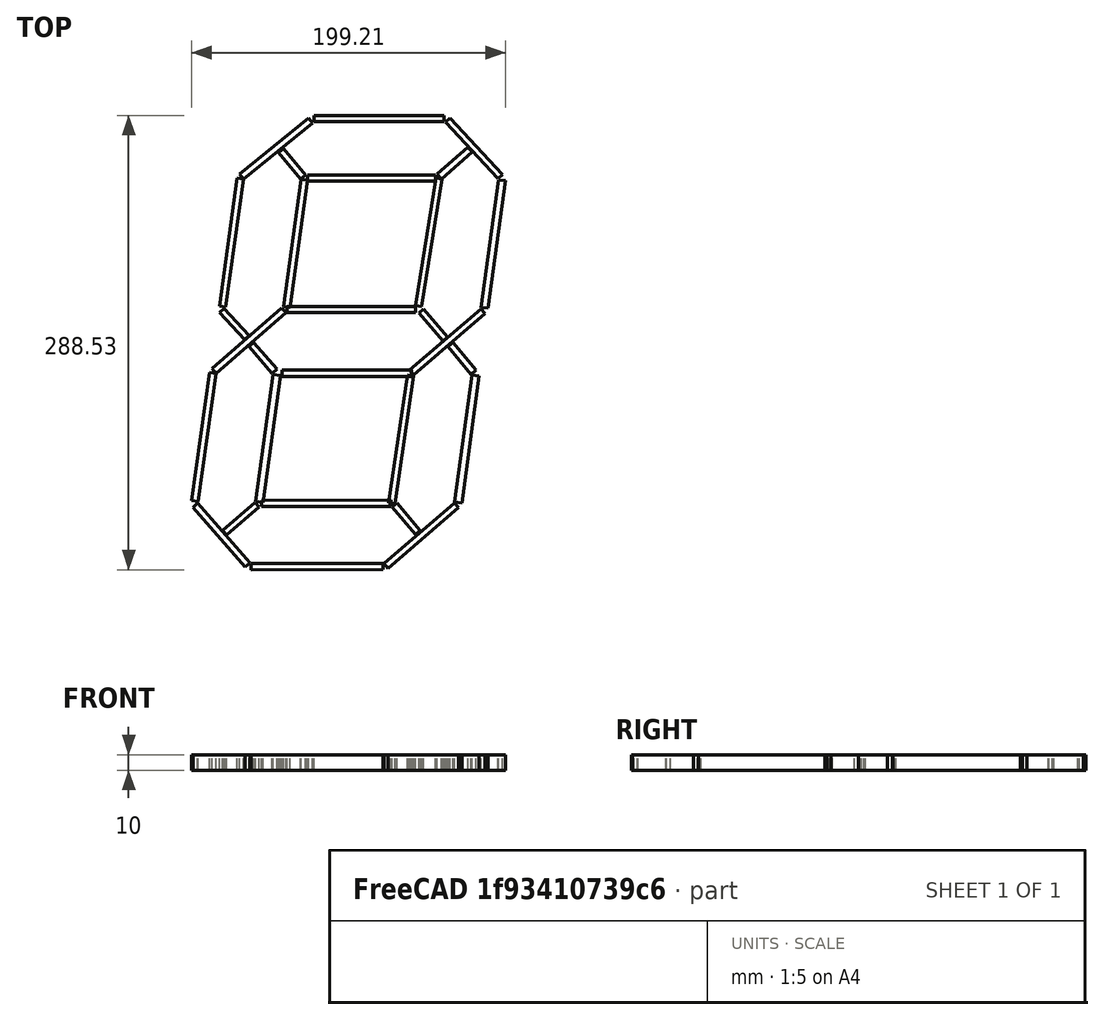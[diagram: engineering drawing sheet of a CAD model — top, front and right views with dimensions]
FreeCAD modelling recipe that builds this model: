
FCSTD DOCUMENT  (FreeCAD 0.18R16131 (Git))
Label: afficheur
License: All rights reserved
LicenseURL: http://en.wikipedia.org/wiki/All_rights_reserved
objects: Image::ImagePlane×1, Sketcher::SketchObject×1, PartDesign::Body×1, Part::Extrusion×1
note: 3 computed .brp shape members not serialized (recipe doc carries the construction recipe); baked Part::Feature solids carry a one-line shape summary decoded from their .brp

FEATURE [Image::ImagePlane] ImagePlane
  XSize = 210
  YSize = 297
FEATURE [Sketcher::SketchObject] Sketch
  MapMode = 5
  Support = -> [XY_Plane]
  sketch-geometry (112):
    g0: LineSegment StartX=-80.0528 StartY=21.6446 StartZ=0 EndX=-68.7891 EndY=102.867 EndZ=0
    g1: LineSegment StartX=-68.7891 StartY=102.867 StartZ=0 EndX=-72.7512 EndY=103.417 EndZ=0
    g2: LineSegment StartX=-72.7512 StartY=103.417 StartZ=0 EndX=-84.0149 EndY=22.1941 EndZ=0
    g3: LineSegment StartX=-84.0149 StartY=22.1941 StartZ=0 EndX=-80.0528 EndY=21.6446 EndZ=0
    g4: LineSegment StartX=-68.7891 StartY=102.867 StartZ=0 EndX=-24.7803 EndY=138.396 EndZ=0
    g5: LineSegment StartX=-24.7803 StartY=138.396 StartZ=0 EndX=-27.2929 EndY=141.508 EndZ=0
    g6: LineSegment StartX=-27.2929 StartY=141.508 StartZ=0 EndX=-71.3017 EndY=105.98 EndZ=0
    g7: LineSegment StartX=-71.3017 StartY=105.98 StartZ=0 EndX=-68.7891 EndY=102.867 EndZ=0
    g8: LineSegment StartX=-97.5888 StartY=-101.804 StartZ=0 EndX=-86.1106 EndY=-20.6108 EndZ=0
    g9: LineSegment StartX=-86.1106 StartY=-20.6108 StartZ=0 EndX=-90.0712 EndY=-20.0509 EndZ=0
    g10: LineSegment StartX=-90.0712 StartY=-20.0509 StartZ=0 EndX=-101.549 EndY=-101.244 EndZ=0
    g11: LineSegment StartX=-101.549 StartY=-101.244 StartZ=0 EndX=-97.5888 EndY=-101.804 EndZ=0
    g12: LineSegment StartX=-86.1106 StartY=-20.6108 StartZ=0 EndX=-41.7841 EndY=18.0739 EndZ=0
    g13: LineSegment StartX=-41.7841 StartY=18.0739 StartZ=0 EndX=-44.4143 EndY=21.0876 EndZ=0
    g14: LineSegment StartX=-44.4143 StartY=21.0876 StartZ=0 EndX=-88.7407 EndY=-17.5971 EndZ=0
    g15: LineSegment StartX=-88.7407 StartY=-17.5971 StartZ=0 EndX=-86.1106 EndY=-20.6108 EndZ=0
    g16: LineSegment StartX=44.4454 StartY=22.0114 StartZ=0 EndX=57.4126 EndY=102.98 EndZ=0
    g17: LineSegment StartX=57.4126 StartY=102.98 StartZ=0 EndX=53.4629 EndY=103.612 EndZ=0
    g18: LineSegment StartX=53.4629 StartY=103.612 StartZ=0 EndX=40.4957 EndY=22.6439 EndZ=0
    g19: LineSegment StartX=40.4957 StartY=22.6439 StartZ=0 EndX=44.4454 EndY=22.0114 EndZ=0
    g20: LineSegment StartX=27.5517 StartY=-103.318 StartZ=0 EndX=39.3566 EndY=-22.1724 EndZ=0
    g21: LineSegment StartX=39.3566 StartY=-22.1724 StartZ=0 EndX=35.3983 EndY=-21.5965 EndZ=0
    g22: LineSegment StartX=35.3983 StartY=-21.5965 StartZ=0 EndX=23.5934 EndY=-102.742 EndZ=0
    g23: LineSegment StartX=23.5934 StartY=-102.742 StartZ=0 EndX=27.5517 EndY=-103.318 EndZ=0
    g24: LineSegment StartX=39.4539 StartY=-21.4329 StartZ=0 EndX=84.758 EndY=17.4459 EndZ=0
    g25: LineSegment StartX=84.758 StartY=17.4459 StartZ=0 EndX=82.153 EndY=20.4814 EndZ=0
    g26: LineSegment StartX=82.153 StartY=20.4814 StartZ=0 EndX=36.8489 EndY=-18.3974 EndZ=0
    g27: LineSegment StartX=36.8489 StartY=-18.3974 StartZ=0 EndX=39.4539 EndY=-21.4329 EndZ=0
    g28: LineSegment StartX=-46.4 StartY=119.697 StartZ=0 EndX=-43.3361 EndY=122.268 EndZ=0
    g29: LineSegment StartX=-43.3361 StartY=122.268 StartZ=0 EndX=-29.2643 EndY=105.501 EndZ=0
    g30: LineSegment StartX=-29.2643 StartY=105.501 StartZ=0 EndX=-32.3282 EndY=102.93 EndZ=0
    g31: LineSegment StartX=-32.3282 StartY=102.93 StartZ=0 EndX=-46.4 EndY=119.697 EndZ=0
    g32: LineSegment StartX=42.7184 StartY=17.7806 StartZ=0 EndX=45.757 EndY=20.382 EndZ=0
    g33: LineSegment StartX=45.757 StartY=20.382 StartZ=0 EndX=60.9792 EndY=2.60137 EndZ=0
    g34: LineSegment StartX=60.9792 StartY=2.60137 StartZ=0 EndX=57.9407 EndY=0 EndZ=0
    g35: LineSegment StartX=57.9407 StartY=0 StartZ=0 EndX=42.7184 EndY=17.7806 EndZ=0
    g36: LineSegment StartX=-65.1983 StartY=-3.41341 StartZ=0 EndX=-62.1657 EndY=-0.805122 EndZ=0
    g37: LineSegment StartX=-62.1657 StartY=-0.805122 StartZ=0 EndX=-47.4642 EndY=-17.8984 EndZ=0
    g38: LineSegment StartX=-47.4642 StartY=-17.8984 StartZ=0 EndX=-50.4969 EndY=-20.5067 EndZ=0
    g39: LineSegment StartX=-50.4969 StartY=-20.5067 StartZ=0 EndX=-65.1983 EndY=-3.41341 EndZ=0
    g40: LineSegment StartX=61.1912 StartY=-3.50708 StartZ=0 EndX=64.2552 EndY=-0.935642 EndZ=0
    g41: LineSegment StartX=64.2552 StartY=-0.935642 StartZ=0 EndX=79.019 EndY=-18.5271 EndZ=0
    g42: LineSegment StartX=79.019 StartY=-18.5271 StartZ=0 EndX=75.955 EndY=-21.0985 EndZ=0
    g43: LineSegment StartX=75.955 StartY=-21.0985 StartZ=0 EndX=61.1912 EndY=-3.50708 EndZ=0
    g44: LineSegment StartX=25.7044 StartY=-105.315 StartZ=0 EndX=28.7683 EndY=-102.743 EndZ=0
    g45: LineSegment StartX=28.7683 StartY=-102.743 StartZ=0 EndX=43.5321 EndY=-120.335 EndZ=0
    g46: LineSegment StartX=43.5321 StartY=-120.335 StartZ=0 EndX=40.4682 EndY=-122.906 EndZ=0
    g47: LineSegment StartX=40.4682 StartY=-122.906 StartZ=0 EndX=25.7044 EndY=-105.315 EndZ=0
    g48: LineSegment StartX=-83.8754 StartY=17.9786 StartZ=0 EndX=-80.9281 EndY=20.683 EndZ=0
    g49: LineSegment StartX=-80.9281 StartY=20.683 StartZ=0 EndX=-65.206 EndY=3.54857 EndZ=0
    g50: LineSegment StartX=-65.206 StartY=3.54857 StartZ=0 EndX=-68.1533 EndY=0.844226 EndZ=0
    g51: LineSegment StartX=-68.1533 StartY=0.844226 StartZ=0 EndX=-83.8754 EndY=17.9786 EndZ=0
    g52: LineSegment StartX=-56.3952 StartY=-102.565 StartZ=0 EndX=-45.2429 EndY=-21.8493 EndZ=0
    g53: LineSegment StartX=-45.2429 StartY=-21.8493 StartZ=0 EndX=-49.8266 EndY=-21.216 EndZ=0
    g54: LineSegment StartX=-49.8266 StartY=-21.216 StartZ=0 EndX=-60.9789 EndY=-101.932 EndZ=0
    g55: LineSegment StartX=-60.9789 StartY=-101.932 StartZ=0 EndX=-56.3952 EndY=-102.565 EndZ=0
    g56: LineSegment StartX=69.9748 StartY=-102.706 StartZ=0 EndX=80.8261 EndY=-22.2952 EndZ=0
    g57: LineSegment StartX=80.8261 StartY=-22.2952 StartZ=0 EndX=76.3147 EndY=-21.6864 EndZ=0
    g58: LineSegment StartX=76.3147 StartY=-21.6864 StartZ=0 EndX=65.4635 EndY=-102.097 EndZ=0
    g59: LineSegment StartX=65.4635 StartY=-102.097 StartZ=0 EndX=69.9748 EndY=-102.706 EndZ=0
    g60: LineSegment StartX=-39.2627 StartY=21.4194 StartZ=0 EndX=-28.1746 EndY=102.11 EndZ=0
    g61: LineSegment StartX=-28.1746 StartY=102.11 StartZ=0 EndX=-32.1374 EndY=102.655 EndZ=0
    g62: LineSegment StartX=-32.1374 StartY=102.655 StartZ=0 EndX=-43.2254 EndY=21.964 EndZ=0
    g63: LineSegment StartX=-43.2254 StartY=21.964 StartZ=0 EndX=-39.2627 EndY=21.4194 EndZ=0
    g64: LineSegment StartX=86.4927 StartY=20.8333 StartZ=0 EndX=97.66 EndY=101.812 EndZ=0
    g65: LineSegment StartX=97.66 StartY=101.812 StartZ=0 EndX=93.3498 EndY=102.406 EndZ=0
    g66: LineSegment StartX=93.3498 StartY=102.406 StartZ=0 EndX=82.1825 EndY=21.4277 EndZ=0
    g67: LineSegment StartX=82.1825 StartY=21.4277 StartZ=0 EndX=86.4927 EndY=20.8333 EndZ=0
    g68: LineSegment StartX=23.1509 StartY=-144.428 StartZ=0 EndX=67.908 EndY=-105.772 EndZ=0
    g69: LineSegment StartX=65.2934 StartY=-102.744 StartZ=0 EndX=20.5363 EndY=-141.401 EndZ=0
    g70: LineSegment StartX=20.5363 StartY=-141.401 StartZ=0 EndX=23.1509 EndY=-144.428 EndZ=0
    g71: LineSegment StartX=67.908 StartY=-105.772 StartZ=0 EndX=65.2934 EndY=-102.744 EndZ=0
    g72: LineSegment StartX=-97.7878 StartY=-102.928 StartZ=0 EndX=-100.805 EndY=-105.554 EndZ=0
    g73: LineSegment StartX=-64.6334 StartY=-141.017 StartZ=0 EndX=-97.7878 EndY=-102.928 EndZ=0
    g74: LineSegment StartX=-100.805 StartY=-105.554 StartZ=0 EndX=-67.6505 EndY=-143.643 EndZ=0
    g75: LineSegment StartX=-67.6505 StartY=-143.643 StartZ=0 EndX=-64.6334 EndY=-141.017 EndZ=0
    g76: LineSegment StartX=-81.926 StartY=-120.298 StartZ=0 EndX=-61.4802 EndY=-102.465 EndZ=0
    g77: LineSegment StartX=-61.4802 StartY=-102.465 StartZ=0 EndX=-58.851 EndY=-105.479 EndZ=0
    g78: LineSegment StartX=-79.2967 StartY=-123.312 StartZ=0 EndX=-81.926 EndY=-120.298 EndZ=0
    g79: LineSegment StartX=-58.851 StartY=-105.479 StartZ=0 EndX=-79.2967 EndY=-123.312 EndZ=0
    g80: LineSegment StartX=59.6818 StartY=138.989 StartZ=0 EndX=92.8609 EndY=103.131 EndZ=0
    g81: LineSegment StartX=95.7969 StartY=105.848 StartZ=0 EndX=62.6177 EndY=141.706 EndZ=0
    g82: LineSegment StartX=62.6177 StartY=141.706 StartZ=0 EndX=59.6818 EndY=138.989 EndZ=0
    g83: LineSegment StartX=92.8609 StartY=103.131 StartZ=0 EndX=95.7969 EndY=105.848 EndZ=0
    g84: LineSegment StartX=-23.9018 StartY=139.268 StartZ=0 EndX=58.5026 EndY=139.294 EndZ=0
    g85: LineSegment StartX=58.5013 StartY=143.294 StartZ=0 EndX=-23.9031 EndY=143.268 EndZ=0
    g86: LineSegment StartX=-23.9031 StartY=143.268 StartZ=0 EndX=-23.9018 EndY=139.268 EndZ=0
    g87: LineSegment StartX=58.5026 StartY=139.294 StartZ=0 EndX=58.5013 EndY=143.294 EndZ=0
    g88: LineSegment StartX=-28.0827 StartY=101.499 StartZ=0 EndX=53.3052 EndY=101.525 EndZ=0
    g89: LineSegment StartX=53.3039 StartY=105.525 StartZ=0 EndX=-28.084 EndY=105.499 EndZ=0
    g90: LineSegment StartX=-28.084 StartY=105.499 StartZ=0 EndX=-28.0827 EndY=101.499 EndZ=0
    g91: LineSegment StartX=53.3052 StartY=101.525 StartZ=0 EndX=53.3039 EndY=105.525 EndZ=0
    g92: LineSegment StartX=-41.057 StartY=18.0798 StartZ=0 EndX=40.6428 EndY=17.9939 EndZ=0
    g93: LineSegment StartX=40.6471 StartY=21.9939 StartZ=0 EndX=-41.0528 EndY=22.0798 EndZ=0
    g94: LineSegment StartX=-41.0528 StartY=22.0798 StartZ=0 EndX=-41.057 EndY=18.0798 EndZ=0
    g95: LineSegment StartX=40.6428 StartY=17.9939 StartZ=0 EndX=40.6471 EndY=21.9939 EndZ=0
    g96: LineSegment StartX=-44.345 StartY=-22.4905 StartZ=0 EndX=38.0594 EndY=-22.464 EndZ=0
    g97: LineSegment StartX=38.0581 StartY=-18.464 StartZ=0 EndX=-44.3463 EndY=-18.4905 EndZ=0
    g98: LineSegment StartX=-44.3463 StartY=-18.4905 StartZ=0 EndX=-44.345 EndY=-22.4905 EndZ=0
    g99: LineSegment StartX=38.0594 StartY=-22.464 StartZ=0 EndX=38.0581 EndY=-18.464 EndZ=0
    g100: LineSegment StartX=-57.3206 StartY=-105.121 StartZ=0 EndX=25.0838 EndY=-105.095 EndZ=0
    g101: LineSegment StartX=25.0825 StartY=-101.095 StartZ=0 EndX=-57.3219 EndY=-101.121 EndZ=0
    g102: LineSegment StartX=-57.3219 StartY=-101.121 StartZ=0 EndX=-57.3206 EndY=-105.121 EndZ=0
    g103: LineSegment StartX=25.0838 StartY=-105.095 StartZ=0 EndX=25.0825 EndY=-101.095 EndZ=0
    g104: LineSegment StartX=-63.9508 StartY=-145.244 StartZ=0 EndX=19.7698 EndY=-145.217 EndZ=0
    g105: LineSegment StartX=19.7685 StartY=-141.217 StartZ=0 EndX=-63.9521 EndY=-141.244 EndZ=0
    g106: LineSegment StartX=-63.9521 StartY=-141.244 StartZ=0 EndX=-63.9508 EndY=-145.244 EndZ=0
    g107: LineSegment StartX=19.7698 StartY=-145.217 StartZ=0 EndX=19.7685 EndY=-141.217 EndZ=0
    g108: LineSegment StartX=54.3488 StartY=106.042 StartZ=0 EndX=73.8695 EndY=123.069 EndZ=0
    g109: LineSegment StartX=56.9781 StartY=103.028 StartZ=0 EndX=54.3488 EndY=106.042 EndZ=0
    g110: LineSegment StartX=76.4987 StartY=120.054 StartZ=0 EndX=56.9781 EndY=103.028 EndZ=0
    g111: LineSegment StartX=73.8695 StartY=123.069 StartZ=0 EndX=76.4987 EndY=120.054 EndZ=0
  constraints (226):
    c: Coincident(g0,g1)
    c: Coincident(g1,g2)
    c: Coincident(g2,g3)
    c: Coincident(g3,g0)
    c: Distance(g0) = 82
    c: Equal(g0,g2)
    c: Distance(g1) = 4
    c: Equal(g1,g3)
    c: Angle(g3,g2) = 1.5708
    c: Coincident(g0,g4)
    c: Coincident(g4,g5)
    c: Coincident(g5,g6)
    c: Coincident(g6,g7)
    c: Coincident(g7,g4)
    c: Angle(g6,g5) = 1.5708
    c: Equal(g6,g4)
    c: Parallel(g7,g5)
    c: Distance(g5) = 4
    c: Coincident(g8,g9)
    c: Coincident(g9,g10)
    c: Coincident(g10,g11)
    c: Coincident(g11,g8)
    c: Equal(g0,g8) = 82
    c: Equal(g8,g10)
    c: Equal(g1,g9) = 4
    c: Equal(g9,g11)
    c: Angle(g11,g10) = 1.5708
    c: Coincident(g8,g12)
    c: Coincident(g12,g13)
    c: Coincident(g13,g14)
    c: Coincident(g14,g15)
    c: Coincident(g15,g12)
    c: Angle(g14,g13) = 1.5708
    c: Equal(g14,g12)
    c: Parallel(g15,g13)
    c: Equal(g5,g13) = 4
    c: Coincident(g16,g17)
    c: Coincident(g17,g18)
    c: Coincident(g18,g19)
    c: Coincident(g19,g16)
    c: Equal(g0,g16) = 82
    c: Equal(g16,g18)
    c: Equal(g1,g17) = 4
    c: Equal(g17,g19)
    c: Angle(g19,g18) = 1.5708
    c: Coincident(g21,g22)
    c: Coincident(g22,g23)
    c: Coincident(g23,g20)
    c: Equal(g16,g20) = 82
    c: Equal(g20,g22)
    c: Equal(g17,g21) = 4
    c: Equal(g21,g23)
    c: Angle(g23,g22) = 1.5708
    c: Coincident(g24,g25)
    c: Coincident(g25,g26)
    c: Coincident(g26,g27)
    c: Coincident(g27,g24)
    c: Angle(g26,g25) = 1.5708
    c: Equal(g26,g24)
    c: Parallel(g27,g25)
    c: Coincident(g28,g29)
    c: Coincident(g29,g30)
    c: Coincident(g30,g31)
    c: Coincident(g31,g28)
    c: Angle(g29,g30) = 1.5708
    c: Equal(g31,g29)
    c: Equal(g28,g30)
    c: Coincident(g32,g33)
    c: Coincident(g33,g34)
    c: Coincident(g34,g35)
    c: Coincident(g35,g32)
    c: Angle(g33,g34) = 1.5708
    c: Equal(g35,g33)
    c: Equal(g32,g34)
    c: PointOnObject(g35,g-1)
    c: Distance(g32) = 4
    c: Distance(g30) = 4
    c: Coincident(g36,g37)
    c: Coincident(g37,g38)
    c: Coincident(g38,g39)
    c: Coincident(g39,g36)
    c: Angle(g37,g38) = 1.5708
    c: Equal(g39,g37)
    c: Equal(g36,g38)
    c: Equal(g30,g38) = 4
    c: Coincident(g40,g41)
    c: Coincident(g41,g42)
    c: Coincident(g42,g43)
    c: Coincident(g43,g40)
    c: Angle(g41,g42) = 1.5708
    c: Equal(g43,g41)
    c: Equal(g40,g42)
    c: Coincident(g44,g45)
    c: Coincident(g45,g46)
    c: Coincident(g46,g47)
    c: Coincident(g47,g44)
    c: Angle(g45,g46) = 1.5708
    c: Equal(g47,g45)
    c: Equal(g44,g46)
    c: Coincident(g48,g49)
    c: Coincident(g49,g50)
    c: Coincident(g50,g51)
    c: Coincident(g51,g48)
    c: Angle(g49,g50) = 1.5708
    c: Equal(g51,g49)
    c: Equal(g48,g50)
    c: Coincident(g52,g53)
    c: Coincident(g53,g54)
    c: Coincident(g54,g55)
    c: Coincident(g55,g52)
    c: Equal(g52,g54)
    c: Equal(g53,g55)
    c: Angle(g55,g54) = 1.5708
    c: Coincident(g56,g57)
    c: Coincident(g57,g58)
    c: Coincident(g58,g59)
    c: Coincident(g59,g56)
    c: Equal(g56,g58)
    c: Equal(g57,g59)
    c: Angle(g59,g58) = 1.5708
    c: Coincident(g60,g61)
    c: Coincident(g61,g62)
    c: Coincident(g62,g63)
    c: Coincident(g63,g60)
    c: Equal(g60,g62)
    c: Equal(g61,g63)
    c: Angle(g63,g62) = 1.5708
    c: Coincident(g64,g65)
    c: Coincident(g65,g66)
    c: Coincident(g66,g67)
    c: Coincident(g67,g64)
    c: Equal(g64,g66)
    c: Equal(g65,g67)
    c: Angle(g67,g66) = 1.5708
    c: Coincident(g68,g71)
    c: Coincident(g71,g69)
    c: Coincident(g69,g70)
    c: Coincident(g70,g68)
    c: Angle(g69,g71) = 1.5708
    c: Equal(g69,g68)
    c: Parallel(g70,g71)
    c: Distance(g70) = 4
    c: Coincident(g73,g72)
    c: Coincident(g72,g74)
    c: Coincident(g74,g75)
    c: Coincident(g75,g73)
    c: Angle(g74,g72) = 1.5708
    c: Equal(g74,g73)
    c: Parallel(g75,g72)
    c: Equal(g70,g75) = 4
    c: Coincident(g77,g79)
    c: Coincident(g79,g78)
    c: Coincident(g78,g76)
    c: Coincident(g76,g77)
    c: Angle(g79,g78) = 1.5708
    c: Equal(g76,g79)
    c: Equal(g77,g78)
    c: Distance(g77) = 4
    c: Distance(g61) = 4
    c: Distance(g48) = 4
    c: Distance(g27) = 4
    c: Coincident(g21,g20)
    c: Coincident(g80,g83)
    c: Coincident(g83,g81)
    c: Coincident(g81,g82)
    c: Coincident(g82,g80)
    c: Angle(g81,g83) = 1.5708
    c: Equal(g81,g80)
    c: Parallel(g82,g83)
    c: Equal(g70,g82) = 4
    c: Coincident(g84,g87)
    c: Coincident(g87,g85)
    c: Coincident(g85,g86)
    c: Coincident(g86,g84)
    c: Angle(g85,g87) = 1.5708
    c: Equal(g85,g84)
    c: Parallel(g86,g87)
    c: Distance(g87) = 4
    c: Coincident(g88,g91)
    c: Coincident(g91,g89)
    c: Coincident(g89,g90)
    c: Coincident(g90,g88)
    c: Angle(g89,g91) = 1.5708
    c: Equal(g89,g88)
    c: Parallel(g90,g91)
    c: Equal(g87,g91) = 4
    c: Coincident(g92,g95)
    c: Coincident(g95,g93)
    c: Coincident(g93,g94)
    c: Coincident(g94,g92)
    c: Angle(g93,g95) = 1.5708
    c: Equal(g93,g92)
    c: Parallel(g94,g95)
    c: Distance(g95) = 4
    c: Coincident(g96,g99)
    c: Coincident(g99,g97)
    c: Coincident(g97,g98)
    c: Coincident(g98,g96)
    c: Angle(g97,g99) = 1.5708
    c: Equal(g97,g96)
    c: Parallel(g98,g99)
    c: Distance(g99) = 4
    c: Coincident(g100,g103)
    c: Coincident(g103,g101)
    c: Coincident(g101,g102)
    c: Coincident(g102,g100)
    c: Angle(g101,g103) = 1.5708
    c: Equal(g101,g100)
    c: Parallel(g102,g103)
    c: Distance(g103) = 4
    c: Coincident(g104,g107)
    c: Coincident(g107,g105)
    c: Coincident(g105,g106)
    c: Coincident(g106,g104)
    c: Angle(g105,g107) = 1.5708
    c: Equal(g105,g104)
    c: Parallel(g106,g107)
    c: Distance(g107) = 4
    c: Coincident(g111,g110)
    c: Coincident(g110,g109)
    c: Coincident(g109,g108)
    c: Coincident(g108,g111)
    c: Angle(g110,g109) = 1.5708
    c: Equal(g108,g110)
    c: Equal(g111,g109)
    c: Distance(g111) = 4
FEATURE [PartDesign::Body] Body
  Group = -> [Sketch]
  Origin = -> Origin
FEATURE [Part::Extrusion] Extrude
  Base = -> Sketch
  Dir = (0,0,1)
  DirMode = 2
  FaceMakerClass = Part::FaceMakerBullseye
  LengthFwd = 22.3
  LengthRev = 0
  Solid = true
  Symmetric = false
